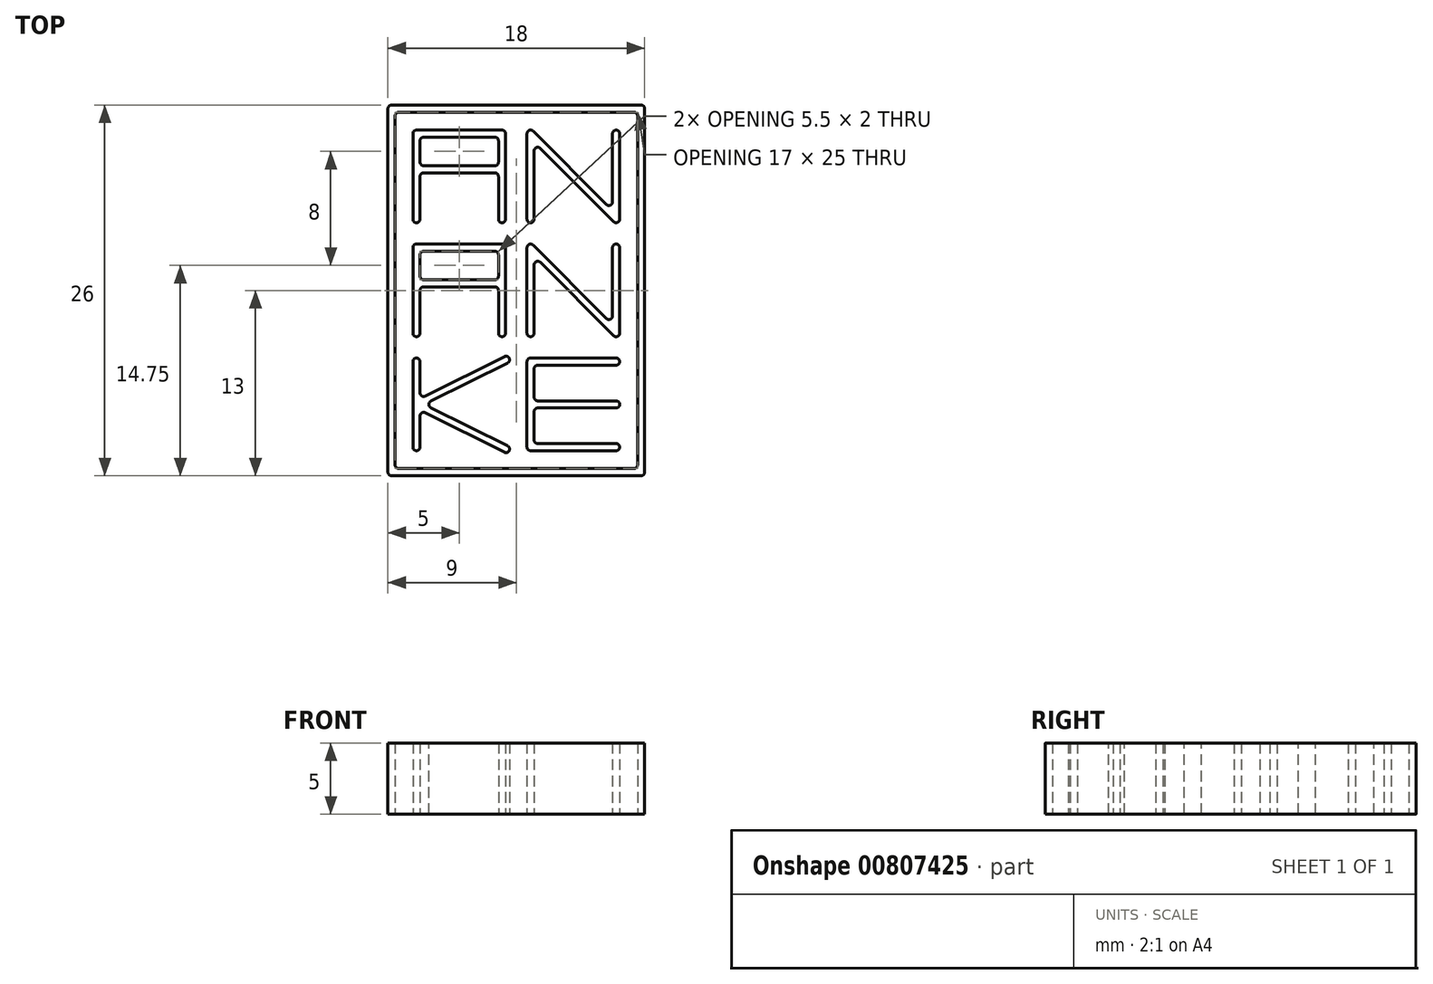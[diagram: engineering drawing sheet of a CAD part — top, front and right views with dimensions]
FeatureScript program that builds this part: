
annotation { "Feature Type Name" : "Feature", "Feature Type Description" : "" }
export const myFeature = defineFeature(function(context is Context, id is Id, definition is map)
    precondition{}
    {
        {
            var Q0;
            Q0=qCreatedBy(makeId("Top.planeOp"),FACE);
            var sketch = newSketch(context, id + "F0", { "sketchPlane" : qUnion([Q0])});
            skLineSegment(sketch, "E0.bottom", {"start": v(-9, 13) * mm, "end": v(9, 13) * mm});
            skLineSegment(sketch, "E0.top", {"start": v(-9, -13) * mm, "end": v(9, -13) * mm});
            skLineSegment(sketch, "E0.left", {"start": v(-9, 13) * mm, "end": v(-9, -13) * mm});
            skLineSegment(sketch, "E0.right", {"start": v(9, 13) * mm, "end": v(9, -13) * mm});
            skPoint(sketch, "E0.middle", {"position": v(0, 0) * mm});
            skLineSegment(sketch, "E1", {"start": v(-1, 8.5) * mm, "end": v(-1, 11) * mm});
            skLineSegment(sketch, "E2", {"start": v(-7, 11) * mm, "end": v(-1, 11) * mm});
            skLineSegment(sketch, "E3", {"start": v(-1, -3) * mm, "end": v(-1, 3) * mm});
            skLineSegment(sketch, "E4", {"start": v(-7, 3) * mm, "end": v(-1, 3) * mm});
            skLineSegment(sketch, "E5", {"start": v(-7, 3) * mm, "end": v(-7, -3) * mm});
            skLineSegment(sketch, "E6", {"start": v(-7, 0.5) * mm, "end": v(-1, 0.5) * mm});
            skLineSegment(sketch, "E7", {"start": v(1, 5) * mm, "end": v(1, 11) * mm});
            skLineSegment(sketch, "E8", {"start": v(1, 11) * mm, "end": v(7, 5) * mm});
            skLineSegment(sketch, "E9", {"start": v(7, 5) * mm, "end": v(7, 11) * mm});
            skLineSegment(sketch, "E10", {"start": v(1, -3) * mm, "end": v(1, 3) * mm});
            skLineSegment(sketch, "E11", {"start": v(1, 3) * mm, "end": v(7, -3) * mm});
            skLineSegment(sketch, "E12", {"start": v(7, -3) * mm, "end": v(7, 3) * mm});
            skLineSegment(sketch, "E13", {"start": v(7, -5) * mm, "end": v(1, -5) * mm});
            skLineSegment(sketch, "E14", {"start": v(1, -5) * mm, "end": v(1, -11) * mm});
            skLineSegment(sketch, "E15", {"start": v(1, -11) * mm, "end": v(7, -11) * mm});
            skLineSegment(sketch, "E16", {"start": v(1, -8) * mm, "end": v(7, -8) * mm});
            skLineSegment(sketch, "E17", {"start": v(7, -5) * mm, "end": v(7, -8) * mm, "construction": true});
            skLineSegment(sketch, "E18", {"start": v(7, -11) * mm, "end": v(7, -8) * mm, "construction": true});
            skLineSegment(sketch, "E19", {"start": v(-7, -3) * mm, "end": v(-1, -3) * mm, "construction": true});
            skLineSegment(sketch, "E20", {"start": v(1, -3) * mm, "end": v(7, -3) * mm, "construction": true});
            skLineSegment(sketch, "E21", {"start": v(7, 3) * mm, "end": v(1, 3) * mm, "construction": true});
            skLineSegment(sketch, "E22", {"start": v(1, 5) * mm, "end": v(7, 5) * mm, "construction": true});
            skLineSegment(sketch, "E23", {"start": v(7, 11) * mm, "end": v(1, 11) * mm, "construction": true});
            skLineSegment(sketch, "E24", {"start": v(-7, 8.5) * mm, "end": v(-7, 11) * mm});
            skLineSegment(sketch, "E25", {"start": v(-7, 5) * mm, "end": v(-7, 11) * mm});
            skLineSegment(sketch, "E26", {"start": v(-1, 11) * mm, "end": v(-1, 5) * mm});
            skLineSegment(sketch, "E27", {"start": v(-7, 8.5) * mm, "end": v(-1, 8.5) * mm});
            skLineSegment(sketch, "E28", {"start": v(-7, 5) * mm, "end": v(-1, 5) * mm, "construction": true});
            skLineSegment(sketch, "E29", {"start": v(-7, -5) * mm, "end": v(-7, -11) * mm});
            skLineSegment(sketch, "E30", {"start": v(-7, -5) * mm, "end": v(-1, -5) * mm, "construction": true});
            skLineSegment(sketch, "E31", {"start": v(-7, -11) * mm, "end": v(-1, -11) * mm, "construction": true});
            skLineSegment(sketch, "E32", {"start": v(-1, -5) * mm, "end": v(-1, -11) * mm, "construction": true});
            skLineSegment(sketch, "E33", {"start": v(-7, -8) * mm, "end": v(-1, -11) * mm});
            skLineSegment(sketch, "E34", {"start": v(-7, -8) * mm, "end": v(-1, -5) * mm});
            skSolve(sketch);
        }
        {
            var Q0;
            Q0=makeQuery(id+"F0.imprint","IMPRINT",FACE,{"disambiguationData":[TD([[makeQuery(id+"F0.imprint","IMPRINT",EDGE,{"derivedFrom":sQuery(id+"F0.wireOp",EDGE,"E0.bottom")}),-1.0]])]});
            var sketch = newSketch(context, id + "F1", { "sketchPlane" : qUnion([Q0])});
            skLineSegment(sketch, "E35.0", {"start": v(-8.75, 12.75) * mm, "end": v(8.75, 12.75) * mm, "construction": true});
            skLineSegment(sketch, "E35.1", {"start": v(-8.75, 12.75) * mm, "end": v(-8.75, -12.75) * mm, "construction": true});
            skLineSegment(sketch, "E35.2", {"start": v(-8.75, -12.75) * mm, "end": v(8.75, -12.75) * mm, "construction": true});
            skLineSegment(sketch, "E35.3", {"start": v(8.75, 12.75) * mm, "end": v(8.75, -12.75) * mm, "construction": true});
            skLineSegment(sketch, "E36.0", {"start": v(-8.5, 12.5) * mm, "end": v(8.5, 12.5) * mm});
            skLineSegment(sketch, "E36.1", {"start": v(-8.5, 12.5) * mm, "end": v(-8.5, -12.5) * mm});
            skLineSegment(sketch, "E36.2", {"start": v(-8.5, -12.5) * mm, "end": v(8.5, -12.5) * mm});
            skLineSegment(sketch, "E36.3", {"start": v(8.5, 12.5) * mm, "end": v(8.5, -12.5) * mm});
            skLineSegment(sketch, "E37.0", {"start": v(-0.75, 11.25) * mm, "end": v(-0.75, 5) * mm});
            skLineSegment(sketch, "E37.1", {"start": v(-7.25, 11.25) * mm, "end": v(-0.75, 11.25) * mm});
            skLineSegment(sketch, "E37.2", {"start": v(-7.25, 5) * mm, "end": v(-7.25, 11.25) * mm});
            skLineSegment(sketch, "E38.0", {"start": v(-1.25, 10.75) * mm, "end": v(-1.25, 8.75) * mm});
            skLineSegment(sketch, "E38.1", {"start": v(-6.75, 10.75) * mm, "end": v(-1.25, 10.75) * mm});
            skLineSegment(sketch, "E38.2", {"start": v(-6.75, 5) * mm, "end": v(-6.75, 8.25) * mm});
            skLineSegment(sketch, "E39", {"start": v(-7.25, 5) * mm, "end": v(-7.25, 4.75) * mm});
            skLineSegment(sketch, "E40", {"start": v(-7.25, 4.75) * mm, "end": v(-6.75, 4.75) * mm});
            skLineSegment(sketch, "E41", {"start": v(-6.75, 4.75) * mm, "end": v(-6.75, 5) * mm});
            skLineSegment(sketch, "E42", {"start": v(-7.25, 5) * mm, "end": v(-6.75, 5) * mm, "construction": true});
            skLineSegment(sketch, "E43", {"start": v(-1.25, 5) * mm, "end": v(-1.25, 4.75) * mm});
            skLineSegment(sketch, "E44", {"start": v(-1.25, 4.75) * mm, "end": v(-0.75, 4.75) * mm});
            skLineSegment(sketch, "E45", {"start": v(-0.75, 4.75) * mm, "end": v(-0.75, 5) * mm});
            skLineSegment(sketch, "E46", {"start": v(-1.25, 5) * mm, "end": v(-0.75, 5) * mm});
            skLineSegment(sketch, "E47.0", {"start": v(-6.75, 8.25) * mm, "end": v(-1.25, 8.25) * mm});
            skLineSegment(sketch, "E48.0", {"start": v(-6.75, 8.75) * mm, "end": v(-1.25, 8.75) * mm});
            skLineSegment(sketch, "E49.trimOffspring", {"start": v(-6.75, 8.75) * mm, "end": v(-6.75, 10.75) * mm});
            skLineSegment(sketch, "E50.trimOffspring", {"start": v(-1.25, 8.25) * mm, "end": v(-1.25, 5) * mm});
            skLineSegment(sketch, "E51.0", {"start": v(6.75, 5.6) * mm, "end": v(6.75, 11) * mm});
            skLineSegment(sketch, "E51.1", {"start": v(0.75, 11.6) * mm, "end": v(6.75, 5.6) * mm});
            skLineSegment(sketch, "E51.2", {"start": v(0.75, 5) * mm, "end": v(0.75, 11.6) * mm});
            skLineSegment(sketch, "E52.0", {"start": v(7.25, 4.4) * mm, "end": v(7.25, 11) * mm});
            skLineSegment(sketch, "E52.1", {"start": v(1.25, 10.4) * mm, "end": v(7.25, 4.4) * mm});
            skLineSegment(sketch, "E52.2", {"start": v(1.25, 5) * mm, "end": v(1.25, 10.4) * mm});
            skLineSegment(sketch, "E53", {"start": v(0.75, 5) * mm, "end": v(1.25, 5) * mm, "construction": true});
            skLineSegment(sketch, "E54", {"start": v(6.75, 11) * mm, "end": v(7.25, 11) * mm, "construction": true});
            skLineSegment(sketch, "E55", {"start": v(0.75, 5) * mm, "end": v(0.75, 4.75) * mm});
            skLineSegment(sketch, "E56", {"start": v(0.75, 4.75) * mm, "end": v(1.25, 4.75) * mm});
            skLineSegment(sketch, "E57", {"start": v(1.25, 4.75) * mm, "end": v(1.25, 5) * mm});
            skLineSegment(sketch, "E58", {"start": v(6.75, 11) * mm, "end": v(6.75, 11.25) * mm});
            skLineSegment(sketch, "E59", {"start": v(6.75, 11.25) * mm, "end": v(7.25, 11.25) * mm});
            skLineSegment(sketch, "E60", {"start": v(7.25, 11.25) * mm, "end": v(7.25, 11) * mm});
            skLineSegment(sketch, "E61.0", {"start": v(-7.25, 3.25) * mm, "end": v(-7.25, -3) * mm});
            skLineSegment(sketch, "E61.1", {"start": v(-7.25, 3.25) * mm, "end": v(-0.75, 3.25) * mm});
            skLineSegment(sketch, "E61.2", {"start": v(-0.75, -3) * mm, "end": v(-0.75, 3.25) * mm});
            skLineSegment(sketch, "E62.0", {"start": v(-6.75, 2.75) * mm, "end": v(-6.75, 0.75) * mm});
            skLineSegment(sketch, "E62.1", {"start": v(-6.75, 2.75) * mm, "end": v(-1.25, 2.75) * mm});
            skLineSegment(sketch, "E62.2", {"start": v(-1.25, -3) * mm, "end": v(-1.25, 0.25) * mm});
            skLineSegment(sketch, "E63", {"start": v(-7.25, -3) * mm, "end": v(-6.75, -3) * mm, "construction": true});
            skLineSegment(sketch, "E64", {"start": v(-1.25, -3) * mm, "end": v(-0.75, -3) * mm, "construction": true});
            skLineSegment(sketch, "E65", {"start": v(-1.25, -3) * mm, "end": v(-1.25, -3.25) * mm});
            skLineSegment(sketch, "E66", {"start": v(-1.25, -3.25) * mm, "end": v(-0.75, -3.25) * mm});
            skLineSegment(sketch, "E67", {"start": v(-0.75, -3.25) * mm, "end": v(-0.75, -3) * mm});
            skLineSegment(sketch, "E68", {"start": v(-7.25, -3) * mm, "end": v(-7.25, -3.25) * mm});
            skLineSegment(sketch, "E69", {"start": v(-7.25, -3.25) * mm, "end": v(-6.75, -3.25) * mm});
            skLineSegment(sketch, "E70", {"start": v(-6.75, -3.25) * mm, "end": v(-6.75, -3) * mm});
            skLineSegment(sketch, "E71.0", {"start": v(-6.75, 0.25) * mm, "end": v(-1.25, 0.25) * mm});
            skLineSegment(sketch, "E72.0", {"start": v(-6.75, 0.75) * mm, "end": v(-1.25, 0.75) * mm});
            skLineSegment(sketch, "E73.trimOffspring", {"start": v(-6.75, 0.25) * mm, "end": v(-6.75, -3) * mm});
            skLineSegment(sketch, "E74.trimOffspring", {"start": v(-1.25, 0.75) * mm, "end": v(-1.25, 2.75) * mm});
            skLineSegment(sketch, "E75.0", {"start": v(7.25, -3.6) * mm, "end": v(7.25, 3) * mm});
            skLineSegment(sketch, "E75.1", {"start": v(1.25, 2.4) * mm, "end": v(7.25, -3.6) * mm});
            skLineSegment(sketch, "E75.2", {"start": v(1.25, -3) * mm, "end": v(1.25, 2.4) * mm});
            skLineSegment(sketch, "E76.0", {"start": v(6.75, -2.4) * mm, "end": v(6.75, 3) * mm});
            skLineSegment(sketch, "E76.1", {"start": v(0.75, 3.6) * mm, "end": v(6.75, -2.4) * mm});
            skLineSegment(sketch, "E76.2", {"start": v(0.75, -3) * mm, "end": v(0.75, 3.6) * mm});
            skLineSegment(sketch, "E77.top", {"start": v(6.75, 3.25) * mm, "end": v(7.25, 3.25) * mm});
            skLineSegment(sketch, "E77.left", {"start": v(6.75, 3) * mm, "end": v(6.75, 3.25) * mm});
            skLineSegment(sketch, "E77.right", {"start": v(7.25, 3) * mm, "end": v(7.25, 3.25) * mm});
            skLineSegment(sketch, "E78", {"start": v(6.75, 3) * mm, "end": v(7.25, 3) * mm, "construction": true});
            skLineSegment(sketch, "E79.bottom", {"start": v(0.75, -3) * mm, "end": v(1.25, -3) * mm, "construction": true});
            skLineSegment(sketch, "E79.top", {"start": v(0.75, -3.25) * mm, "end": v(1.25, -3.25) * mm});
            skLineSegment(sketch, "E79.left", {"start": v(0.75, -3) * mm, "end": v(0.75, -3.25) * mm});
            skLineSegment(sketch, "E79.right", {"start": v(1.25, -3) * mm, "end": v(1.25, -3.25) * mm});
            skLineSegment(sketch, "E80.0", {"start": v(0.75, -11.25) * mm, "end": v(7, -11.25) * mm});
            skLineSegment(sketch, "E80.1", {"start": v(0.75, -4.75) * mm, "end": v(0.75, -11.25) * mm});
            skLineSegment(sketch, "E80.2", {"start": v(7, -4.75) * mm, "end": v(0.75, -4.75) * mm});
            skLineSegment(sketch, "E81.0", {"start": v(1.25, -10.75) * mm, "end": v(7, -10.75) * mm});
            skLineSegment(sketch, "E81.1", {"start": v(1.25, -5.25) * mm, "end": v(1.25, -7.75) * mm});
            skLineSegment(sketch, "E81.2", {"start": v(7, -5.25) * mm, "end": v(1.25, -5.25) * mm});
            skLineSegment(sketch, "E82.bottom", {"start": v(7, -4.75) * mm, "end": v(7.25, -4.75) * mm});
            skLineSegment(sketch, "E82.top", {"start": v(7, -5.25) * mm, "end": v(7.25, -5.25) * mm});
            skLineSegment(sketch, "E82.left", {"start": v(7, -4.75) * mm, "end": v(7, -5.25) * mm, "construction": true});
            skLineSegment(sketch, "E82.right", {"start": v(7.25, -4.75) * mm, "end": v(7.25, -5.25) * mm});
            skLineSegment(sketch, "E83.bottom", {"start": v(7, -10.75) * mm, "end": v(7.25, -10.75) * mm});
            skLineSegment(sketch, "E83.top", {"start": v(7, -11.25) * mm, "end": v(7.25, -11.25) * mm});
            skLineSegment(sketch, "E83.left", {"start": v(7, -10.75) * mm, "end": v(7, -11.25) * mm, "construction": true});
            skLineSegment(sketch, "E83.right", {"start": v(7.25, -10.75) * mm, "end": v(7.25, -11.25) * mm});
            skLineSegment(sketch, "E84", {"start": v(1.25, -7.75) * mm, "end": v(7.25, -7.75) * mm});
            skLineSegment(sketch, "E85", {"start": v(7.25, -7.75) * mm, "end": v(7.25, -8.25) * mm});
            skLineSegment(sketch, "E86", {"start": v(7.25, -8.25) * mm, "end": v(1.25, -8.25) * mm});
            skLineSegment(sketch, "E87.trimOffspring", {"start": v(1.25, -8.25) * mm, "end": v(1.25, -10.75) * mm});
            skLineSegment(sketch, "E88.bottom", {"start": v(-7.25, -4.75) * mm, "end": v(-6.75, -4.75) * mm});
            skLineSegment(sketch, "E88.top", {"start": v(-7.25, -11.25) * mm, "end": v(-6.75, -11.25) * mm});
            skLineSegment(sketch, "E88.left", {"start": v(-7.25, -4.75) * mm, "end": v(-7.25, -11.25) * mm});
            skLineSegment(sketch, "E88.right", {"start": v(-6.75, -4.75) * mm, "end": v(-6.75, -7.6) * mm});
            skLineSegment(sketch, "E89", {"start": v(-6.75, -7.6) * mm, "end": v(-0.61, -4.53) * mm});
            skLineSegment(sketch, "E90", {"start": v(-0.61, -4.53) * mm, "end": v(-0.39, -4.97) * mm});
            skLineSegment(sketch, "E91", {"start": v(-0.39, -4.97) * mm, "end": v(-6.44, -8) * mm});
            skLineSegment(sketch, "E92", {"start": v(-6.44, -8) * mm, "end": v(-0.39, -11.03) * mm});
            skLineSegment(sketch, "E93", {"start": v(-0.39, -11.03) * mm, "end": v(-0.61, -11.47) * mm});
            skLineSegment(sketch, "E94", {"start": v(-0.61, -11.47) * mm, "end": v(-6.75, -8.4) * mm});
            skLineSegment(sketch, "E95.trimOffspring", {"start": v(-6.75, -8.4) * mm, "end": v(-6.75, -11.25) * mm});
            skLineSegment(sketch, "E96.0", {"start": v(-9, -13) * mm, "end": v(9, -13) * mm});
            skLineSegment(sketch, "E96.1", {"start": v(-9, 13) * mm, "end": v(-9, -13) * mm});
            skLineSegment(sketch, "E96.2", {"start": v(-9, 13) * mm, "end": v(9, 13) * mm});
            skLineSegment(sketch, "E96.3", {"start": v(9, 13) * mm, "end": v(9, -13) * mm});
            skLineSegment(sketch, "E97", {"start": v(-6.75, -8.4) * mm, "end": v(-6.75, -7.6) * mm, "construction": true});
            skLineSegment(sketch, "E98", {"start": v(-6.75, -8) * mm, "end": v(-7.25, -8) * mm, "construction": true});
            skLineSegment(sketch, "E99", {"start": v(-0.5, -11.25) * mm, "end": v(-6.75, -11.25) * mm, "construction": true});
            skLineSegment(sketch, "E100", {"start": v(-0.5, -4.75) * mm, "end": v(-6.75, -4.75) * mm, "construction": true});
            skLineSegment(sketch, "E101", {"start": v(-6.44, -8) * mm, "end": v(-6.75, -8) * mm, "construction": true});
            skSolve(sketch);
        }
        {
            var Q0;
            Q0 = qSketchRegion(id + "F1", true);
            var Q1;
            Q1=makeQuery(id+"F1.imprint","IMPRINT",FACE,{"disambiguationData":[TD([[makeQuery(id+"F1.imprint","IMPRINT",EDGE,{"derivedFrom":sQuery(id+"F1.wireOp",EDGE,"E37.0")}),-1.0]])]});
            var Q2;
            Q2=makeQuery(id+"F1.imprint","IMPRINT",FACE,{"disambiguationData":[TD([[makeQuery(id+"F1.imprint","IMPRINT",EDGE,{"derivedFrom":sQuery(id+"F1.wireOp",EDGE,"E43")}),1.0]])]});
            var Q3;
            Q3=makeQuery(id+"F1.imprint","IMPRINT",FACE,{"disambiguationData":[TD([[makeQuery(id+"F1.imprint","IMPRINT",EDGE,{"derivedFrom":sQuery(id+"F1.wireOp",EDGE,"E51.0")}),-1.0]])]});
            var Q4;
            Q4=makeQuery(id+"F1.imprint","IMPRINT",FACE,{"disambiguationData":[TD([[makeQuery(id+"F1.imprint","IMPRINT",EDGE,{"derivedFrom":sQuery(id+"F1.wireOp",EDGE,"E75.0")}),1.0]])]});
            var Q5;
            Q5=makeQuery(id+"F1.imprint","IMPRINT",FACE,{"disambiguationData":[TD([[makeQuery(id+"F1.imprint","IMPRINT",EDGE,{"derivedFrom":sQuery(id+"F1.wireOp",EDGE,"E61.0")}),1.0]])]});
            var Q6;
            Q6=makeQuery(id+"F1.imprint","IMPRINT",FACE,{"disambiguationData":[TD([[makeQuery(id+"F1.imprint","IMPRINT",EDGE,{"derivedFrom":sQuery(id+"F1.wireOp",EDGE,"E62.0")}),-1.0]])]});
            var Q7;
            Q7=makeQuery(id+"F1.imprint","IMPRINT",FACE,{"disambiguationData":[TD([[makeQuery(id+"F1.imprint","IMPRINT",EDGE,{"derivedFrom":sQuery(id+"F1.wireOp",EDGE,"E38.0")}),1.0]])]});
            var Q8;
            Q8=makeQuery(id+"F1.imprint","IMPRINT",FACE,{"disambiguationData":[TD([[makeQuery(id+"F1.imprint","IMPRINT",EDGE,{"derivedFrom":sQuery(id+"F1.wireOp",EDGE,"E80.0")}),1.0]])]});
            var Q9;
            Q9=makeQuery(id+"F1.imprint","IMPRINT",FACE,{"disambiguationData":[TD([[makeQuery(id+"F1.imprint","IMPRINT",EDGE,{"derivedFrom":sQuery(id+"F1.wireOp",EDGE,"E88.bottom")}),-1.0]])]});
            extrude(context, id + "F2", {"entities" : qUnion([Q0, Q1, Q2, Q3, Q4, Q5, Q6, Q7, Q8, Q9]), "depth" : 5 * mm, "offsetDistance" : 25 * mm});
        }
        {
            var Q0;
            Q0=makeQuery(id+"F2.opExtrude","SWEPT_EDGE",EDGE,{"disambiguationData":[OSD([sQuery(id+"F1.wireOp",EDGE,"E96.2"),sQuery(id+"F1.wireOp",EDGE,"E96.3")])]});
            var Q1;
            Q1=makeQuery(id+"F2.opExtrude","SWEPT_EDGE",EDGE,{"disambiguationData":[OSD([sQuery(id+"F1.wireOp",EDGE,"E96.1"),sQuery(id+"F1.wireOp",EDGE,"E96.2")])]});
            var Q2;
            Q2=makeQuery(id+"F2.opExtrude","SWEPT_EDGE",EDGE,{"disambiguationData":[OSD([sQuery(id+"F1.wireOp",EDGE,"E36.0"),sQuery(id+"F1.wireOp",EDGE,"E36.3")])]});
            var Q3;
            Q3=makeQuery(id+"F2.opExtrude","SWEPT_EDGE",EDGE,{"disambiguationData":[OSD([sQuery(id+"F1.wireOp",EDGE,"E36.0"),sQuery(id+"F1.wireOp",EDGE,"E36.1")])]});
            var Q4;
            Q4=makeQuery(id+"F2.opExtrude","SWEPT_EDGE",EDGE,{"disambiguationData":[OSD([sQuery(id+"F1.wireOp",EDGE,"E96.0"),sQuery(id+"F1.wireOp",EDGE,"E96.3")])]});
            var Q5;
            Q5=makeQuery(id+"F2.opExtrude","SWEPT_EDGE",EDGE,{"disambiguationData":[OSD([sQuery(id+"F1.wireOp",EDGE,"E96.0"),sQuery(id+"F1.wireOp",EDGE,"E96.1")])]});
            var Q6;
            Q6=makeQuery(id+"F2.opExtrude","SWEPT_EDGE",EDGE,{"disambiguationData":[OSD([sQuery(id+"F1.wireOp",EDGE,"E36.2"),sQuery(id+"F1.wireOp",EDGE,"E36.3")])]});
            var Q7;
            Q7=makeQuery(id+"F2.opExtrude","SWEPT_EDGE",EDGE,{"disambiguationData":[OSD([sQuery(id+"F1.wireOp",EDGE,"E36.1"),sQuery(id+"F1.wireOp",EDGE,"E36.2")])]});
            fillet(context, id + "F3", {"entities" : qUnion([Q0, Q1, Q2, Q3, Q4, Q5, Q6, Q7]), "radius" : 0.25 * mm, "tangentPropagation" : true, "allowEdgeOverflow" : false});
        }
        {
            var Q0;
            Q0=makeQuery(id+"F2.opExtrude","SWEPT_EDGE",EDGE,{"disambiguationData":[OSD([sQuery(id+"F1.wireOp",EDGE,"E38.1"),sQuery(id+"F1.wireOp",EDGE,"E49.trimOffspring")])]});
            var Q1;
            Q1=makeQuery(id+"F2.opExtrude","SWEPT_EDGE",EDGE,{"disambiguationData":[OSD([sQuery(id+"F1.wireOp",EDGE,"E38.2"),sQuery(id+"F1.wireOp",EDGE,"E47.0")])]});
            var Q2;
            Q2=makeQuery(id+"F2.opExtrude","SWEPT_EDGE",EDGE,{"disambiguationData":[OSD([sQuery(id+"F1.wireOp",EDGE,"E40"),sQuery(id+"F1.wireOp",EDGE,"E41")])]});
            var Q3;
            Q3=makeQuery(id+"F2.opExtrude","SWEPT_EDGE",EDGE,{"disambiguationData":[OSD([sQuery(id+"F1.wireOp",EDGE,"E44"),sQuery(id+"F1.wireOp",EDGE,"E45")])]});
            var Q4;
            Q4=makeQuery(id+"F2.opExtrude","SWEPT_EDGE",EDGE,{"disambiguationData":[OSD([sQuery(id+"F1.wireOp",EDGE,"E39"),sQuery(id+"F1.wireOp",EDGE,"E40")])]});
            var Q5;
            Q5=makeQuery(id+"F2.opExtrude","SWEPT_EDGE",EDGE,{"disambiguationData":[OSD([sQuery(id+"F1.wireOp",EDGE,"E43"),sQuery(id+"F1.wireOp",EDGE,"E44")])]});
            var Q6;
            Q6=makeQuery(id+"F2.opExtrude","SWEPT_EDGE",EDGE,{"disambiguationData":[OSD([sQuery(id+"F1.wireOp",EDGE,"E37.0"),sQuery(id+"F1.wireOp",EDGE,"E37.1")])]});
            var Q7;
            Q7=makeQuery(id+"F2.opExtrude","SWEPT_EDGE",EDGE,{"disambiguationData":[OSD([sQuery(id+"F1.wireOp",EDGE,"E38.0"),sQuery(id+"F1.wireOp",EDGE,"E38.1")])]});
            var Q8;
            Q8=makeQuery(id+"F2.opExtrude","SWEPT_EDGE",EDGE,{"disambiguationData":[OSD([sQuery(id+"F1.wireOp",EDGE,"E47.0"),sQuery(id+"F1.wireOp",EDGE,"E50.trimOffspring")])]});
            var Q9;
            Q9=makeQuery(id+"F2.opExtrude","SWEPT_EDGE",EDGE,{"disambiguationData":[OSD([sQuery(id+"F1.wireOp",EDGE,"E37.1"),sQuery(id+"F1.wireOp",EDGE,"E37.2")])]});
            var Q10;
            Q10=makeQuery(id+"F2.opExtrude","SWEPT_EDGE",EDGE,{"disambiguationData":[OSD([sQuery(id+"F1.wireOp",EDGE,"E38.0"),sQuery(id+"F1.wireOp",EDGE,"E48.0")])]});
            var Q11;
            Q11=makeQuery(id+"F2.opExtrude","SWEPT_EDGE",EDGE,{"disambiguationData":[OSD([sQuery(id+"F1.wireOp",EDGE,"E48.0"),sQuery(id+"F1.wireOp",EDGE,"E49.trimOffspring")])]});
            fillet(context, id + "F4", {"entities" : qUnion([Q0, Q1, Q2, Q3, Q4, Q5, Q6, Q7, Q8, Q9, Q10, Q11]), "radius" : 0.25 * mm, "tangentPropagation" : true, "allowEdgeOverflow" : false});
        }
        {
            var Q0;
            Q0=makeQuery(id+"F2.opExtrude","SWEPT_EDGE",EDGE,{"disambiguationData":[OSD([sQuery(id+"F1.wireOp",EDGE,"E59"),sQuery(id+"F1.wireOp",EDGE,"E60")])]});
            var Q1;
            Q1=makeQuery(id+"F2.opExtrude","SWEPT_EDGE",EDGE,{"disambiguationData":[OSD([sQuery(id+"F1.wireOp",EDGE,"E58"),sQuery(id+"F1.wireOp",EDGE,"E59")])]});
            var Q2;
            Q2=makeQuery(id+"F2.opExtrude","SWEPT_EDGE",EDGE,{"disambiguationData":[OSD([sQuery(id+"F1.wireOp",EDGE,"E51.1"),sQuery(id+"F1.wireOp",EDGE,"E51.2")])]});
            var Q3;
            Q3=makeQuery(id+"F2.opExtrude","SWEPT_EDGE",EDGE,{"disambiguationData":[OSD([sQuery(id+"F1.wireOp",EDGE,"E52.0"),sQuery(id+"F1.wireOp",EDGE,"E52.1")])]});
            var Q4;
            Q4=makeQuery(id+"F2.opExtrude","SWEPT_EDGE",EDGE,{"disambiguationData":[OSD([sQuery(id+"F1.wireOp",EDGE,"E56"),sQuery(id+"F1.wireOp",EDGE,"E57")])]});
            var Q5;
            Q5=makeQuery(id+"F2.opExtrude","SWEPT_EDGE",EDGE,{"disambiguationData":[OSD([sQuery(id+"F1.wireOp",EDGE,"E55"),sQuery(id+"F1.wireOp",EDGE,"E56")])]});
            var Q6;
            Q6=makeQuery(id+"F2.opExtrude","SWEPT_EDGE",EDGE,{"disambiguationData":[OSD([sQuery(id+"F1.wireOp",EDGE,"E51.0"),sQuery(id+"F1.wireOp",EDGE,"E51.1")])]});
            var Q7;
            Q7=makeQuery(id+"F2.opExtrude","SWEPT_EDGE",EDGE,{"disambiguationData":[OSD([sQuery(id+"F1.wireOp",EDGE,"E52.1"),sQuery(id+"F1.wireOp",EDGE,"E52.2")])]});
            fillet(context, id + "F5", {"entities" : qUnion([Q0, Q1, Q2, Q3, Q4, Q5, Q6, Q7]), "radius" : 0.25 * mm, "tangentPropagation" : true, "allowEdgeOverflow" : false});
        }
        {
            var Q0;
            Q0=makeQuery(id+"F2.opExtrude","SWEPT_EDGE",EDGE,{"disambiguationData":[OSD([sQuery(id+"F1.wireOp",EDGE,"E75.0"),sQuery(id+"F1.wireOp",EDGE,"E75.1")])]});
            var Q1;
            Q1=makeQuery(id+"F2.opExtrude","SWEPT_EDGE",EDGE,{"disambiguationData":[OSD([sQuery(id+"F1.wireOp",EDGE,"E79.top"),sQuery(id+"F1.wireOp",EDGE,"E79.right")])]});
            var Q2;
            Q2=makeQuery(id+"F2.opExtrude","SWEPT_EDGE",EDGE,{"disambiguationData":[OSD([sQuery(id+"F1.wireOp",EDGE,"E79.top"),sQuery(id+"F1.wireOp",EDGE,"E79.left")])]});
            var Q3;
            Q3=makeQuery(id+"F2.opExtrude","SWEPT_EDGE",EDGE,{"disambiguationData":[OSD([sQuery(id+"F1.wireOp",EDGE,"E77.top"),sQuery(id+"F1.wireOp",EDGE,"E77.right")])]});
            var Q4;
            Q4=makeQuery(id+"F2.opExtrude","SWEPT_EDGE",EDGE,{"disambiguationData":[OSD([sQuery(id+"F1.wireOp",EDGE,"E75.1"),sQuery(id+"F1.wireOp",EDGE,"E75.2")])]});
            var Q5;
            Q5=makeQuery(id+"F2.opExtrude","SWEPT_EDGE",EDGE,{"disambiguationData":[OSD([sQuery(id+"F1.wireOp",EDGE,"E76.1"),sQuery(id+"F1.wireOp",EDGE,"E76.2")])]});
            var Q6;
            Q6=makeQuery(id+"F2.opExtrude","SWEPT_EDGE",EDGE,{"disambiguationData":[OSD([sQuery(id+"F1.wireOp",EDGE,"E77.top"),sQuery(id+"F1.wireOp",EDGE,"E77.left")])]});
            var Q7;
            Q7=makeQuery(id+"F2.opExtrude","SWEPT_EDGE",EDGE,{"disambiguationData":[OSD([sQuery(id+"F1.wireOp",EDGE,"E76.0"),sQuery(id+"F1.wireOp",EDGE,"E76.1")])]});
            fillet(context, id + "F6", {"entities" : qUnion([Q0, Q1, Q2, Q3, Q4, Q5, Q6, Q7]), "radius" : 0.25 * mm, "tangentPropagation" : true, "allowEdgeOverflow" : false});
        }
        {
            var Q0;
            Q0=makeQuery(id+"F2.opExtrude","SWEPT_EDGE",EDGE,{"disambiguationData":[OSD([sQuery(id+"F1.wireOp",EDGE,"E61.1"),sQuery(id+"F1.wireOp",EDGE,"E61.2")])]});
            var Q1;
            Q1=makeQuery(id+"F2.opExtrude","SWEPT_EDGE",EDGE,{"disambiguationData":[OSD([sQuery(id+"F1.wireOp",EDGE,"E61.0"),sQuery(id+"F1.wireOp",EDGE,"E61.1")])]});
            var Q2;
            Q2=makeQuery(id+"F2.opExtrude","SWEPT_EDGE",EDGE,{"disambiguationData":[OSD([sQuery(id+"F1.wireOp",EDGE,"E68"),sQuery(id+"F1.wireOp",EDGE,"E69")])]});
            var Q3;
            Q3=makeQuery(id+"F2.opExtrude","SWEPT_EDGE",EDGE,{"disambiguationData":[OSD([sQuery(id+"F1.wireOp",EDGE,"E65"),sQuery(id+"F1.wireOp",EDGE,"E66")])]});
            var Q4;
            Q4=makeQuery(id+"F2.opExtrude","SWEPT_EDGE",EDGE,{"disambiguationData":[OSD([sQuery(id+"F1.wireOp",EDGE,"E72.0"),sQuery(id+"F1.wireOp",EDGE,"E74.trimOffspring")])]});
            var Q5;
            Q5=makeQuery(id+"F2.opExtrude","SWEPT_EDGE",EDGE,{"disambiguationData":[OSD([sQuery(id+"F1.wireOp",EDGE,"E62.0"),sQuery(id+"F1.wireOp",EDGE,"E72.0")])]});
            var Q6;
            Q6=makeQuery(id+"F2.opExtrude","SWEPT_EDGE",EDGE,{"disambiguationData":[OSD([sQuery(id+"F1.wireOp",EDGE,"E62.2"),sQuery(id+"F1.wireOp",EDGE,"E71.0")])]});
            var Q7;
            Q7=makeQuery(id+"F2.opExtrude","SWEPT_EDGE",EDGE,{"disambiguationData":[OSD([sQuery(id+"F1.wireOp",EDGE,"E71.0"),sQuery(id+"F1.wireOp",EDGE,"E73.trimOffspring")])]});
            var Q8;
            Q8=makeQuery(id+"F2.opExtrude","SWEPT_EDGE",EDGE,{"disambiguationData":[OSD([sQuery(id+"F1.wireOp",EDGE,"E69"),sQuery(id+"F1.wireOp",EDGE,"E70")])]});
            var Q9;
            Q9=makeQuery(id+"F2.opExtrude","SWEPT_EDGE",EDGE,{"disambiguationData":[OSD([sQuery(id+"F1.wireOp",EDGE,"E62.0"),sQuery(id+"F1.wireOp",EDGE,"E62.1")])]});
            var Q10;
            Q10=makeQuery(id+"F2.opExtrude","SWEPT_EDGE",EDGE,{"disambiguationData":[OSD([sQuery(id+"F1.wireOp",EDGE,"E62.1"),sQuery(id+"F1.wireOp",EDGE,"E74.trimOffspring")])]});
            var Q11;
            Q11=makeQuery(id+"F2.opExtrude","SWEPT_EDGE",EDGE,{"disambiguationData":[OSD([sQuery(id+"F1.wireOp",EDGE,"E66"),sQuery(id+"F1.wireOp",EDGE,"E67")])]});
            fillet(context, id + "F7", {"entities" : qUnion([Q0, Q1, Q2, Q3, Q4, Q5, Q6, Q7, Q8, Q9, Q10, Q11]), "radius" : 0.25 * mm, "tangentPropagation" : true, "allowEdgeOverflow" : false});
        }
        {
            var Q0;
            Q0=makeQuery(id+"F2.opExtrude","SWEPT_EDGE",EDGE,{"disambiguationData":[OSD([sQuery(id+"F1.wireOp",EDGE,"E81.1"),sQuery(id+"F1.wireOp",EDGE,"E81.2")])]});
            var Q1;
            Q1=makeQuery(id+"F2.opExtrude","SWEPT_EDGE",EDGE,{"disambiguationData":[OSD([sQuery(id+"F1.wireOp",EDGE,"E82.top"),sQuery(id+"F1.wireOp",EDGE,"E82.right")])]});
            var Q2;
            Q2=makeQuery(id+"F2.opExtrude","SWEPT_EDGE",EDGE,{"disambiguationData":[OSD([sQuery(id+"F1.wireOp",EDGE,"E82.bottom"),sQuery(id+"F1.wireOp",EDGE,"E82.right")])]});
            var Q3;
            Q3=makeQuery(id+"F2.opExtrude","SWEPT_EDGE",EDGE,{"disambiguationData":[OSD([sQuery(id+"F1.wireOp",EDGE,"E85"),sQuery(id+"F1.wireOp",EDGE,"E86")])]});
            var Q4;
            Q4=makeQuery(id+"F2.opExtrude","SWEPT_EDGE",EDGE,{"disambiguationData":[OSD([sQuery(id+"F1.wireOp",EDGE,"E84"),sQuery(id+"F1.wireOp",EDGE,"E85")])]});
            var Q5;
            Q5=makeQuery(id+"F2.opExtrude","SWEPT_EDGE",EDGE,{"disambiguationData":[OSD([sQuery(id+"F1.wireOp",EDGE,"E86"),sQuery(id+"F1.wireOp",EDGE,"E87.trimOffspring")])]});
            var Q6;
            Q6=makeQuery(id+"F2.opExtrude","SWEPT_EDGE",EDGE,{"disambiguationData":[OSD([sQuery(id+"F1.wireOp",EDGE,"E83.top"),sQuery(id+"F1.wireOp",EDGE,"E83.right")])]});
            var Q7;
            Q7=makeQuery(id+"F2.opExtrude","SWEPT_EDGE",EDGE,{"disambiguationData":[OSD([sQuery(id+"F1.wireOp",EDGE,"E83.bottom"),sQuery(id+"F1.wireOp",EDGE,"E83.right")])]});
            var Q8;
            Q8=makeQuery(id+"F2.opExtrude","SWEPT_EDGE",EDGE,{"disambiguationData":[OSD([sQuery(id+"F1.wireOp",EDGE,"E80.0"),sQuery(id+"F1.wireOp",EDGE,"E80.1")])]});
            var Q9;
            Q9=makeQuery(id+"F2.opExtrude","SWEPT_EDGE",EDGE,{"disambiguationData":[OSD([sQuery(id+"F1.wireOp",EDGE,"E81.0"),sQuery(id+"F1.wireOp",EDGE,"E87.trimOffspring")])]});
            var Q10;
            Q10=makeQuery(id+"F2.opExtrude","SWEPT_EDGE",EDGE,{"disambiguationData":[OSD([sQuery(id+"F1.wireOp",EDGE,"E81.1"),sQuery(id+"F1.wireOp",EDGE,"E84")])]});
            var Q11;
            Q11=makeQuery(id+"F2.opExtrude","SWEPT_EDGE",EDGE,{"disambiguationData":[OSD([sQuery(id+"F1.wireOp",EDGE,"E80.1"),sQuery(id+"F1.wireOp",EDGE,"E80.2")])]});
            fillet(context, id + "F8", {"entities" : qUnion([Q0, Q1, Q2, Q3, Q4, Q5, Q6, Q7, Q8, Q9, Q10, Q11]), "radius" : 0.25 * mm, "tangentPropagation" : true, "allowEdgeOverflow" : false});
        }
        {
            var Q0;
            Q0=makeQuery(id+"F2.opExtrude","SWEPT_EDGE",EDGE,{"disambiguationData":[OSD([sQuery(id+"F1.wireOp",EDGE,"E91"),sQuery(id+"F1.wireOp",EDGE,"E92")])]});
            var Q1;
            Q1=makeQuery(id+"F2.opExtrude","SWEPT_EDGE",EDGE,{"disambiguationData":[OSD([sQuery(id+"F1.wireOp",EDGE,"E90"),sQuery(id+"F1.wireOp",EDGE,"E91")])]});
            var Q2;
            Q2=makeQuery(id+"F2.opExtrude","SWEPT_EDGE",EDGE,{"disambiguationData":[OSD([sQuery(id+"F1.wireOp",EDGE,"E89"),sQuery(id+"F1.wireOp",EDGE,"E90")])]});
            var Q3;
            Q3=makeQuery(id+"F2.opExtrude","SWEPT_EDGE",EDGE,{"disambiguationData":[OSD([sQuery(id+"F1.wireOp",EDGE,"E92"),sQuery(id+"F1.wireOp",EDGE,"E93")])]});
            var Q4;
            Q4=makeQuery(id+"F2.opExtrude","SWEPT_EDGE",EDGE,{"disambiguationData":[OSD([sQuery(id+"F1.wireOp",EDGE,"E88.top"),sQuery(id+"F1.wireOp",EDGE,"E95.trimOffspring")])]});
            var Q5;
            Q5=makeQuery(id+"F2.opExtrude","SWEPT_EDGE",EDGE,{"disambiguationData":[OSD([sQuery(id+"F1.wireOp",EDGE,"E88.top"),sQuery(id+"F1.wireOp",EDGE,"E88.left")])]});
            var Q6;
            Q6=makeQuery(id+"F2.opExtrude","SWEPT_EDGE",EDGE,{"disambiguationData":[OSD([sQuery(id+"F1.wireOp",EDGE,"E88.bottom"),sQuery(id+"F1.wireOp",EDGE,"E88.right")])]});
            var Q7;
            Q7=makeQuery(id+"F2.opExtrude","SWEPT_EDGE",EDGE,{"disambiguationData":[OSD([sQuery(id+"F1.wireOp",EDGE,"E93"),sQuery(id+"F1.wireOp",EDGE,"E94")])]});
            var Q8;
            Q8=makeQuery(id+"F2.opExtrude","SWEPT_EDGE",EDGE,{"disambiguationData":[OSD([sQuery(id+"F1.wireOp",EDGE,"E94"),sQuery(id+"F1.wireOp",EDGE,"E95.trimOffspring")])]});
            var Q9;
            Q9=makeQuery(id+"F2.opExtrude","SWEPT_EDGE",EDGE,{"disambiguationData":[OSD([sQuery(id+"F1.wireOp",EDGE,"E88.right"),sQuery(id+"F1.wireOp",EDGE,"E89")])]});
            var Q10;
            Q10=makeQuery(id+"F2.opExtrude","SWEPT_EDGE",EDGE,{"disambiguationData":[OSD([sQuery(id+"F1.wireOp",EDGE,"E88.bottom"),sQuery(id+"F1.wireOp",EDGE,"E88.left")])]});
            fillet(context, id + "F9", {"entities" : qUnion([Q0, Q1, Q2, Q3, Q4, Q5, Q6, Q7, Q8, Q9, Q10]), "radius" : 0.25 * mm, "tangentPropagation" : true, "allowEdgeOverflow" : false});
        }
    });
